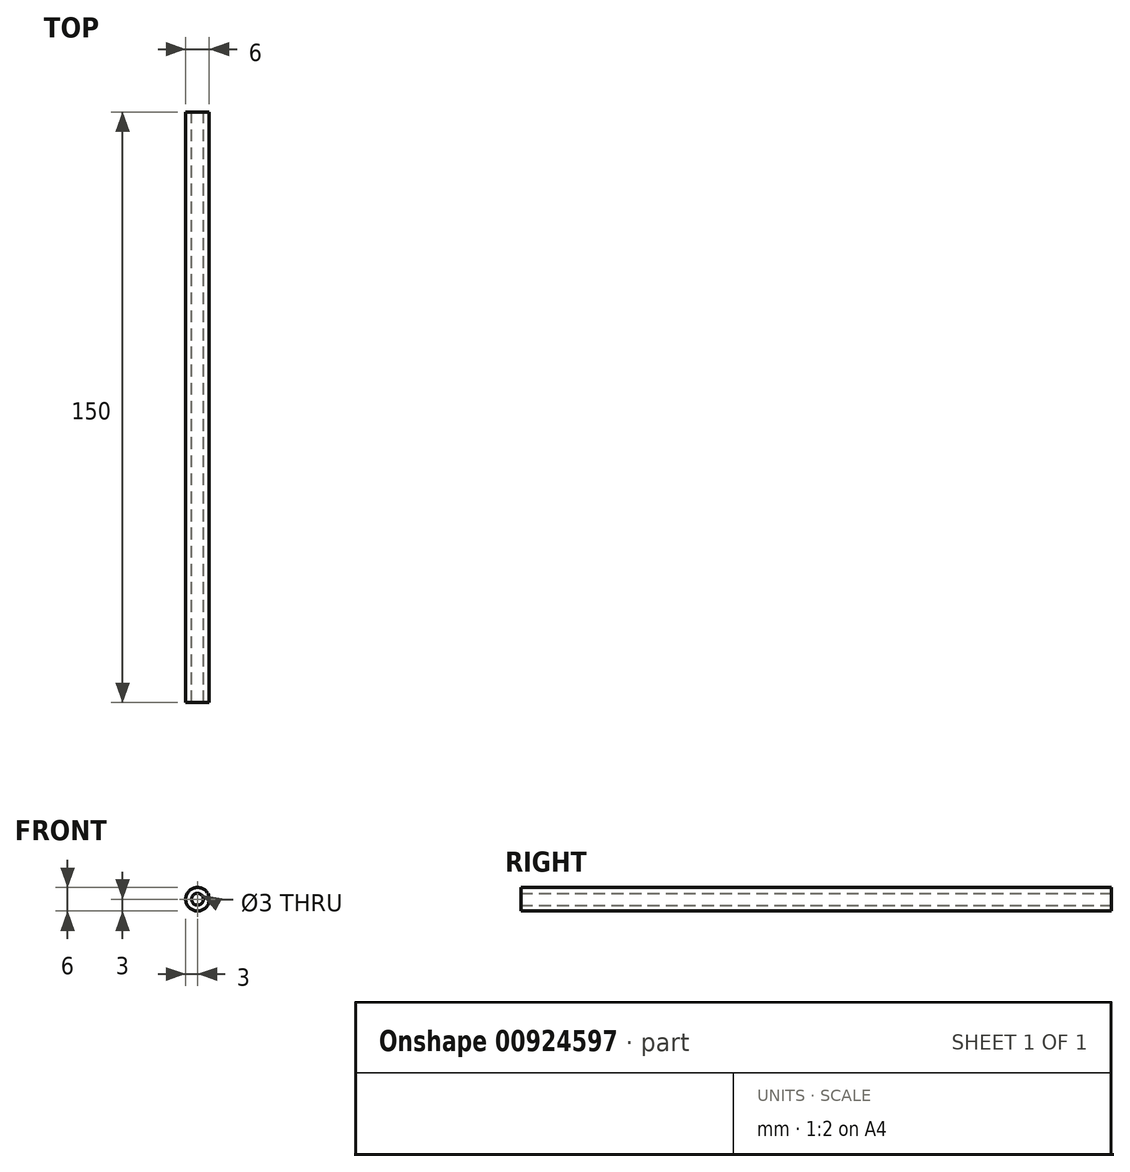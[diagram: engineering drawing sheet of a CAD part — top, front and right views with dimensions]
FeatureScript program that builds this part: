
annotation { "Feature Type Name" : "Feature", "Feature Type Description" : "" }
export const myFeature = defineFeature(function(context is Context, id is Id, definition is map)
    precondition{}
    {
        {
            var Q0;
            Q0=qCreatedBy(makeId("Front.planeOp"),FACE);
            var sketch = newSketch(context, id + "F0", { "sketchPlane" : qUnion([Q0])});
            skCircle(sketch, "E0", {"center": v(0, 0) * mm, "radius": 3 * mm});
            skCircle(sketch, "E1", {"center": v(0, 0) * mm, "radius": 1.5 * mm});
            skSolve(sketch);
        }
        {
            var Q0;
            Q0=makeQuery(id+"F0.imprint","IMPRINT",FACE,{"disambiguationData":[TD([[makeQuery(id+"F0.imprint","IMPRINT",EDGE,{"derivedFrom":sQuery(id+"F0.wireOp",EDGE,"E0")}),1.0]])]});
            extrude(context, id + "F1", {"entities" : qUnion([Q0]), "depth" : 150 * mm, "offsetDistance" : 25 * mm});
        }
    });
